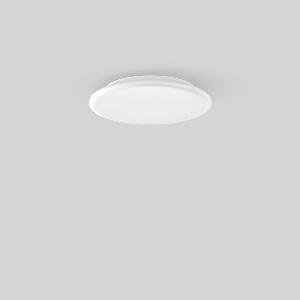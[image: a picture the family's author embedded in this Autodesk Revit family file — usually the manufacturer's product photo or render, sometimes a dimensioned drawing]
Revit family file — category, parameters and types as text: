
# Revit family: hb_501_221174_002_2_6356
name_source: partatom
category: Lighting Fixtures
units: mm (PartAtom-declared; Revit-internal decimal feet)

## family parameters
Cut with Voids When Loaded = No
Host = Face
Light Source = No
Part Type = Normal
Room Calculation Point = No
Round Connector Dimension = Use Diameter
Shared = No

## types (1)
- MultiColor 840 (1 x LED Modul 840, 1100 lm, 4000)
    Apparent Load = 12 VA
    CIE Flux Codes = 45 76 94 98 100
    Color Rendering = 80
    Color Temperature = 4000
    Default Elevation = 1800 mm
    Description = Series: HB 501
Flat decorative round LED surface-mounted luminaire. Housing: plastic (polycarbonate). Diffuser: plastic (polycarbonate), opal. Base and diffuser are sealed together. MultiColour: Colour temperature adjustable via switching element for 3000 K (factory setting), 4000 K and 5700 K. Quick mounting adapter steel sheet, white powder-coated, with bayonet fastening. Driver integrated. 
Colour: white
Diameter: 250 mm
Height: 48 mm
Lamp: LED
Socket: without socket
Colour temperature: 3000K, 4000K, 5700K
Colour rendering index (CRI): 80
System power: 12 W
Rated luminous flux: 1100 lm
Luminous efficiency: 92 lm/W
System power 2: 12 W
Rated luminous flux 2: 1100 lm
Luminous efficiency 2: 92 lm/W
System power 3: 12 W
Rated luminous flux 3: 1100 lm
Luminous efficiency 3: 92 lm/W
Control gear: EB
Protection class: I
Type of protection: IP 40
    Height = 48 mm  [stored 0.15748 ft]
    Lamp = 1 x LED Modul 840
    Lamp Light Flux = 1100 lm
    Lamp count = 1
    Length = 250 mm
    Lifetime = 50000 h
    Luminous efficacy = 92 lm/W
    Manufacturer = RZB
    ModVariant = No
    Model = 221174.002.2
    Mounting Place = Ceiling, Wall
    Mounting Type = Surface mounted
    Number of Poles = 1
    OnlyDefault = Yes
    Power Factor = 1
    Product Name = HB 501
    Product group = Surface mounted ceiling and wall luminaires
    ProductGroupID = 305
    Protection Class = Protection class I
    Protection Degree = IP 40
    RLX_Detail_Level = 1
    RLX_Emergency_Light_Flux = 0 lm
    RLX_Emergency_Type = 0
    RLX_Emergency_Type_DB = No
    RlxData = <blob elided: 129549 chars, md5=78191430>
    Socket = socket
    Standby Power = 0 W
    System Light Flux = 1100 lm
    System Power = 12 W
    Type Comments = MultiColor 840
    Type Image = 221174.002.jpg
    URL = http://relux.com
    VarID = multicolor_840
    Voltage = 230 V
    Voltage Range = 220-240 V
    Weight = 0.00 kg
    Width = 0 mm  [stored 0 ft]

note: [stored X ft] marks values corroborated as IEEE doubles in the binary element streams (Revit-internal decimal feet)

## geometry (parser evidence)
native form markers: Blend x4, Sweep x12
no freeform markers — native parametric forms only
